# Revit family: BE_66453_de_DE
name_source: partatom
category: Leuchten
revit_build: Autodesk Revit 2015 (Build: 20150704_0715(x64)
units: mm (PartAtom-declared; Revit-internal decimal feet)

## types (4) — shared parameters
AC/DC = AC/DC
Aktualisierung = 2016-03-16T04:08:46
BEGA_Dummy = Nein
BEGA_IES = Ja
BEGA_Intern = Ja
BEGA_Intern_Konstruktion = Ja
BEGA_Intern_an = Ja
BEGA_Intern_aus = Ja
Befestigungsabstand = 85 mm
Befestigungsbohrung = Ø 5,5 mm
Beschreibung = Wandleuchte
Beschreibung_Sonderanfertigung = Hier können Sie Informationen zur Sonderanfertigung eintragen.
CE_Konformität = ja
ENEC = ja
Energieeffizienzklasse = LED A++ - A
Farbwiedergabeindex = Ra > 80
Frequenz = 0/50-60 Hz
Gewicht = 4.8 kg
Hersteller = BEGA
Lampe = LED 14 W
Lastklassifizierung = Beleuchtung
Lebensdauerkriterien = L70 = 50.000 h
Logo = BEGA_Logo.png
M_W = Nein
Material_02 = BEGA_Oberfläche_Silber_matt
Material_06 = BEGA_Oberfläche_Edelstahl_gebürstet
Material_09 = BEGA_Glas_klar
Material_15 = BEGA_Leuchtmedium_matt
Material_17 = BEGA_Reflektor
Produktdatenblatt = http://www.bega.de
Scheinlast = 0 VA
Schutzart = IP 66
Schutzklasse = I
Sonderanfertigung = Nein
Spannung = 0 V
Typenbild = 66453.png
URL = http://www.bega.de
zero-valued in all types: Vorgabe-Ansicht

## per-type parameters (varying)
| type | BEGA_IES1 | BEGA_IES2 | Bestellnummer | Farbtemperatur | LED_Modulbezeichnung | Lampenlichtstrom | Leuchtenlichtstrom | M_A | M_G | Modell |
| BEGA_66453_Grafit_K4 | Nein | Ja | 66453 | 4000 K | 2x LED-0410/840 | 1930 lm | 1566 lm | Nein | Ja | 66453 |
| BEGA_66453_Grafit_K3 | Ja | Nein | 66453K3 | 3000 K | 2x LED-0410/830 | 1810 lm | 1468 lm | Nein | Ja | 66453K3 |
| BEGA_66453_Silber_K4 | Nein | Ja | 66453A | 4000 K | 2x LED-0410/840 | 1930 lm | 1566 lm | Ja | Nein | 66453A |
| BEGA_66453_Silber_K3 | Ja | Nein | 66453AK3 | 3000 K | 2x LED-0410/830 | 1810 lm | 1468 lm | Ja | Nein | 66453AK3 |

## geometry (parser evidence)
native form markers: Sweep x8
no freeform markers — native parametric forms only
